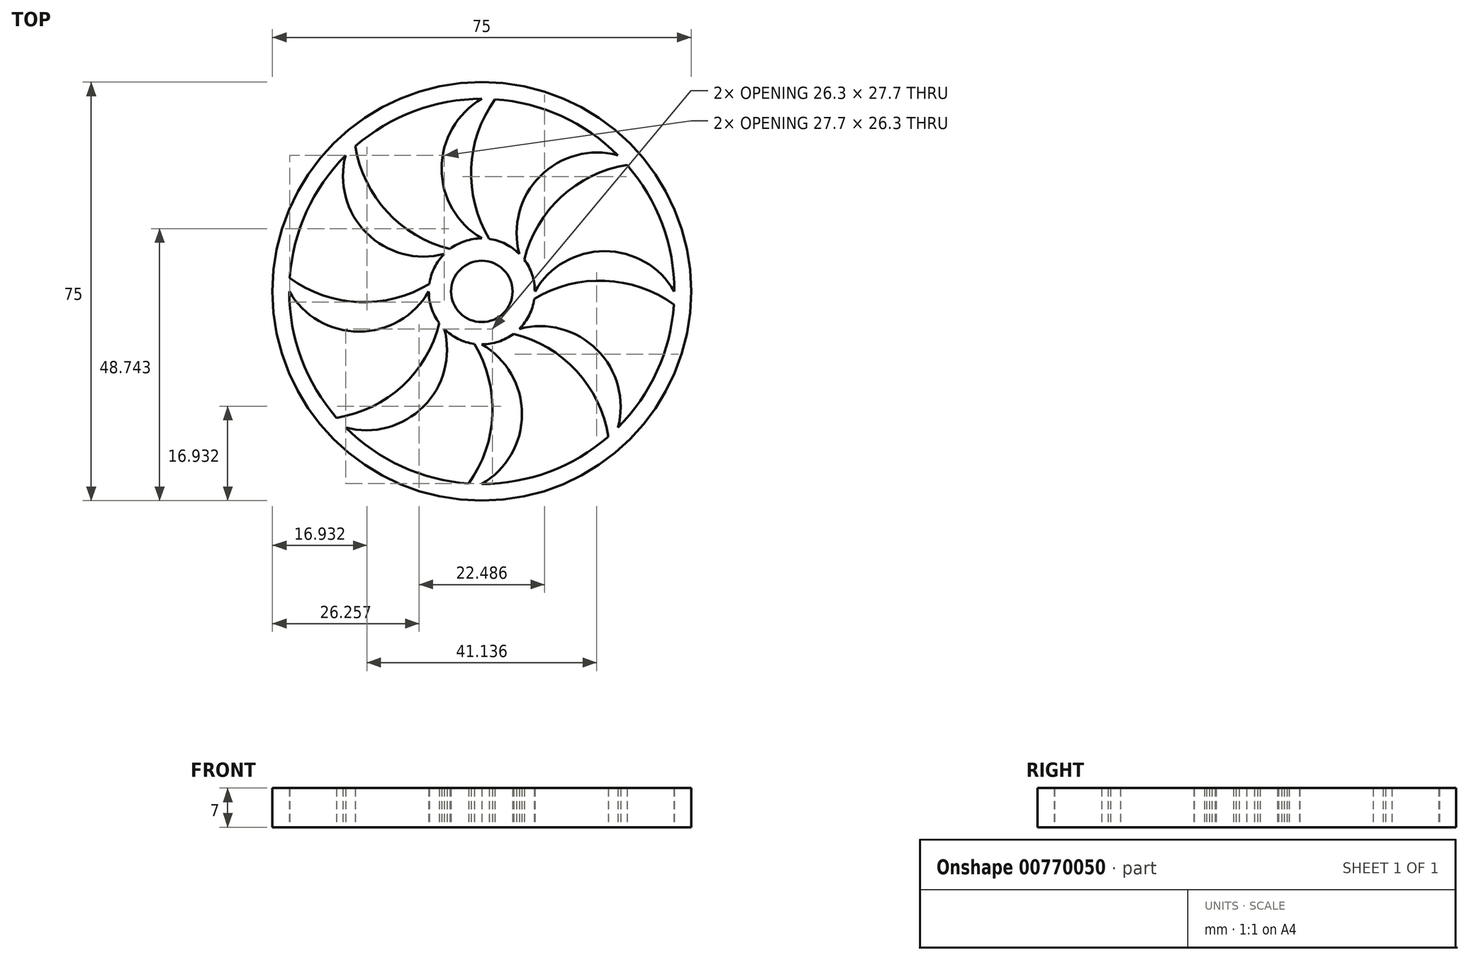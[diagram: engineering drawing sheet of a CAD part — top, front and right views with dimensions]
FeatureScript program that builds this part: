
annotation { "Feature Type Name" : "Feature", "Feature Type Description" : "" }
export const myFeature = defineFeature(function(context is Context, id is Id, definition is map)
    precondition{}
    {
        {
            var Q0;
            Q0=qCreatedBy(makeId("Top.planeOp"),FACE);
            var sketch = newSketch(context, id + "F0", { "sketchPlane" : qUnion([Q0])});
            skArc(sketch, "E0", {"start": v(9.5, 0) * mm, "mid": v(9.01, 3) * mm, "end": v(7.6, 5.7) * mm, "construction": true});
            skCircle(sketch, "E1", {"center": v(0, 0) * mm, "radius": 37.5 * mm});
            skArc(sketch, "E2", {"start": v(34.5, 0) * mm, "mid": v(32.3, 12.1) * mm, "end": v(26.02, 22.66) * mm});
            skArc(sketch, "E3", {"start": v(34.5, 0) * mm, "mid": v(22, 7.2) * mm, "end": v(9.5, 0) * mm});
            skArc(sketch, "E4", {"start": v(34.42, -2.38) * mm, "mid": v(22.07, 1.9) * mm, "end": v(9.4, -1.35) * mm});
            skArc(sketch, "E5.1.0", {"start": v(24.4, 24.4) * mm, "mid": v(10.46, 20.65) * mm, "end": v(6.72, 6.72) * mm});
            skArc(sketch, "E5.1.1", {"start": v(26.02, 22.66) * mm, "mid": v(14.25, 16.95) * mm, "end": v(7.6, 5.7) * mm});
            skArc(sketch, "E5.2.0", {"start": v(0, 34.5) * mm, "mid": v(-7.2, 22) * mm, "end": v(0, 9.5) * mm});
            skArc(sketch, "E5.2.1", {"start": v(2.38, 34.42) * mm, "mid": v(-1.9, 22.07) * mm, "end": v(1.35, 9.4) * mm});
            skArc(sketch, "E5.3.0", {"start": v(-24.4, 24.4) * mm, "mid": v(-20.65, 10.46) * mm, "end": v(-6.72, 6.72) * mm});
            skArc(sketch, "E5.3.1", {"start": v(-22.66, 26.02) * mm, "mid": v(-16.95, 14.25) * mm, "end": v(-5.7, 7.6) * mm});
            skArc(sketch, "E5.4.0", {"start": v(-34.5, 0) * mm, "mid": v(-22, -7.2) * mm, "end": v(-9.5, 0) * mm});
            skArc(sketch, "E5.4.1", {"start": v(-34.42, 2.38) * mm, "mid": v(-22.07, -1.9) * mm, "end": v(-9.4, 1.35) * mm});
            skArc(sketch, "E5.5.0", {"start": v(-24.4, -24.4) * mm, "mid": v(-10.46, -20.65) * mm, "end": v(-6.72, -6.72) * mm});
            skArc(sketch, "E5.5.1", {"start": v(-26.02, -22.66) * mm, "mid": v(-14.25, -16.95) * mm, "end": v(-7.6, -5.7) * mm});
            skArc(sketch, "E5.6.0", {"start": v(0, -34.5) * mm, "mid": v(7.2, -22) * mm, "end": v(0, -9.5) * mm});
            skArc(sketch, "E5.6.1", {"start": v(-2.38, -34.42) * mm, "mid": v(1.9, -22.07) * mm, "end": v(-1.35, -9.4) * mm});
            skArc(sketch, "E5.7.0", {"start": v(24.4, -24.4) * mm, "mid": v(20.65, -10.46) * mm, "end": v(6.72, -6.72) * mm});
            skArc(sketch, "E5.7.1", {"start": v(22.66, -26.02) * mm, "mid": v(16.95, -14.25) * mm, "end": v(5.7, -7.6) * mm});
            skArc(sketch, "E6", {"start": v(9.5, 0) * mm, "mid": v(9.01, 3) * mm, "end": v(7.6, 5.7) * mm});
            skArc(sketch, "E7.trimOffspring", {"start": v(24.4, -24.4) * mm, "mid": v(31.4, -14.3) * mm, "end": v(34.42, -2.38) * mm});
            skArc(sketch, "E8.trimOffspring", {"start": v(0, -34.5) * mm, "mid": v(12.1, -32.3) * mm, "end": v(22.66, -26.02) * mm});
            skArc(sketch, "E9.trimOffspring", {"start": v(24.4, 24.4) * mm, "mid": v(14.3, 31.4) * mm, "end": v(2.38, 34.42) * mm});
            skArc(sketch, "E10.trimOffspring", {"start": v(0, 34.5) * mm, "mid": v(-12.1, 32.3) * mm, "end": v(-22.66, 26.02) * mm});
            skArc(sketch, "E11.trimOffspring", {"start": v(-24.4, 24.4) * mm, "mid": v(-31.4, 14.3) * mm, "end": v(-34.42, 2.38) * mm});
            skArc(sketch, "E12.trimOffspring", {"start": v(-34.5, 0) * mm, "mid": v(-32.3, -12.1) * mm, "end": v(-26.02, -22.66) * mm});
            skArc(sketch, "E13.trimOffspring", {"start": v(-24.4, -24.4) * mm, "mid": v(-14.3, -31.4) * mm, "end": v(-2.38, -34.42) * mm});
            skArc(sketch, "E14.trimOffspring", {"start": v(6.72, 6.72) * mm, "mid": v(4.25, 8.5) * mm, "end": v(1.35, 9.4) * mm, "construction": true});
            skArc(sketch, "E15.trimOffspring", {"start": v(6.72, 6.72) * mm, "mid": v(4.25, 8.5) * mm, "end": v(1.35, 9.4) * mm});
            skArc(sketch, "E16.trimOffspring", {"start": v(0, 9.5) * mm, "mid": v(-3, 9.01) * mm, "end": v(-5.7, 7.6) * mm, "construction": true});
            skArc(sketch, "E17.trimOffspring", {"start": v(0, 9.5) * mm, "mid": v(-3, 9.01) * mm, "end": v(-5.7, 7.6) * mm});
            skArc(sketch, "E18.trimOffspring", {"start": v(-6.72, 6.72) * mm, "mid": v(-8.5, 4.25) * mm, "end": v(-9.4, 1.35) * mm, "construction": true});
            skArc(sketch, "E19.trimOffspring", {"start": v(-6.72, 6.72) * mm, "mid": v(-8.5, 4.25) * mm, "end": v(-9.4, 1.35) * mm});
            skArc(sketch, "E20.trimOffspring", {"start": v(-9.5, 0) * mm, "mid": v(-9.01, -3) * mm, "end": v(-7.6, -5.7) * mm, "construction": true});
            skArc(sketch, "E21.trimOffspring", {"start": v(-9.5, 0) * mm, "mid": v(-9.01, -3) * mm, "end": v(-7.6, -5.7) * mm});
            skArc(sketch, "E22.trimOffspring", {"start": v(-6.72, -6.72) * mm, "mid": v(-4.25, -8.5) * mm, "end": v(-1.35, -9.4) * mm, "construction": true});
            skArc(sketch, "E23.trimOffspring", {"start": v(-6.72, -6.72) * mm, "mid": v(-4.25, -8.5) * mm, "end": v(-1.35, -9.4) * mm});
            skArc(sketch, "E24.trimOffspring", {"start": v(0, -9.5) * mm, "mid": v(3, -9.01) * mm, "end": v(5.7, -7.6) * mm, "construction": true});
            skArc(sketch, "E25.trimOffspring", {"start": v(0, -9.5) * mm, "mid": v(3, -9.01) * mm, "end": v(5.7, -7.6) * mm});
            skArc(sketch, "E26.trimOffspring", {"start": v(6.72, -6.72) * mm, "mid": v(8.5, -4.25) * mm, "end": v(9.4, -1.35) * mm, "construction": true});
            skArc(sketch, "E27.trimOffspring", {"start": v(6.72, -6.72) * mm, "mid": v(8.5, -4.25) * mm, "end": v(9.4, -1.35) * mm});
            skCircle(sketch, "E28", {"center": v(0, 0) * mm, "radius": 5.5 * mm});
            skSolve(sketch);
        }
        {
            var Q0;
            Q0=makeQuery(id+"F0.imprint","IMPRINT",FACE,{"disambiguationData":[TD([[makeQuery(id+"F0.imprint","IMPRINT",EDGE,{"derivedFrom":sQuery(id+"F0.wireOp",EDGE,"E1")}),1.0]])]});
            extrude(context, id + "F1", {"entities" : qUnion([Q0]), "depth" : 7 * mm, "offsetDistance" : 25 * mm});
        }
    });
